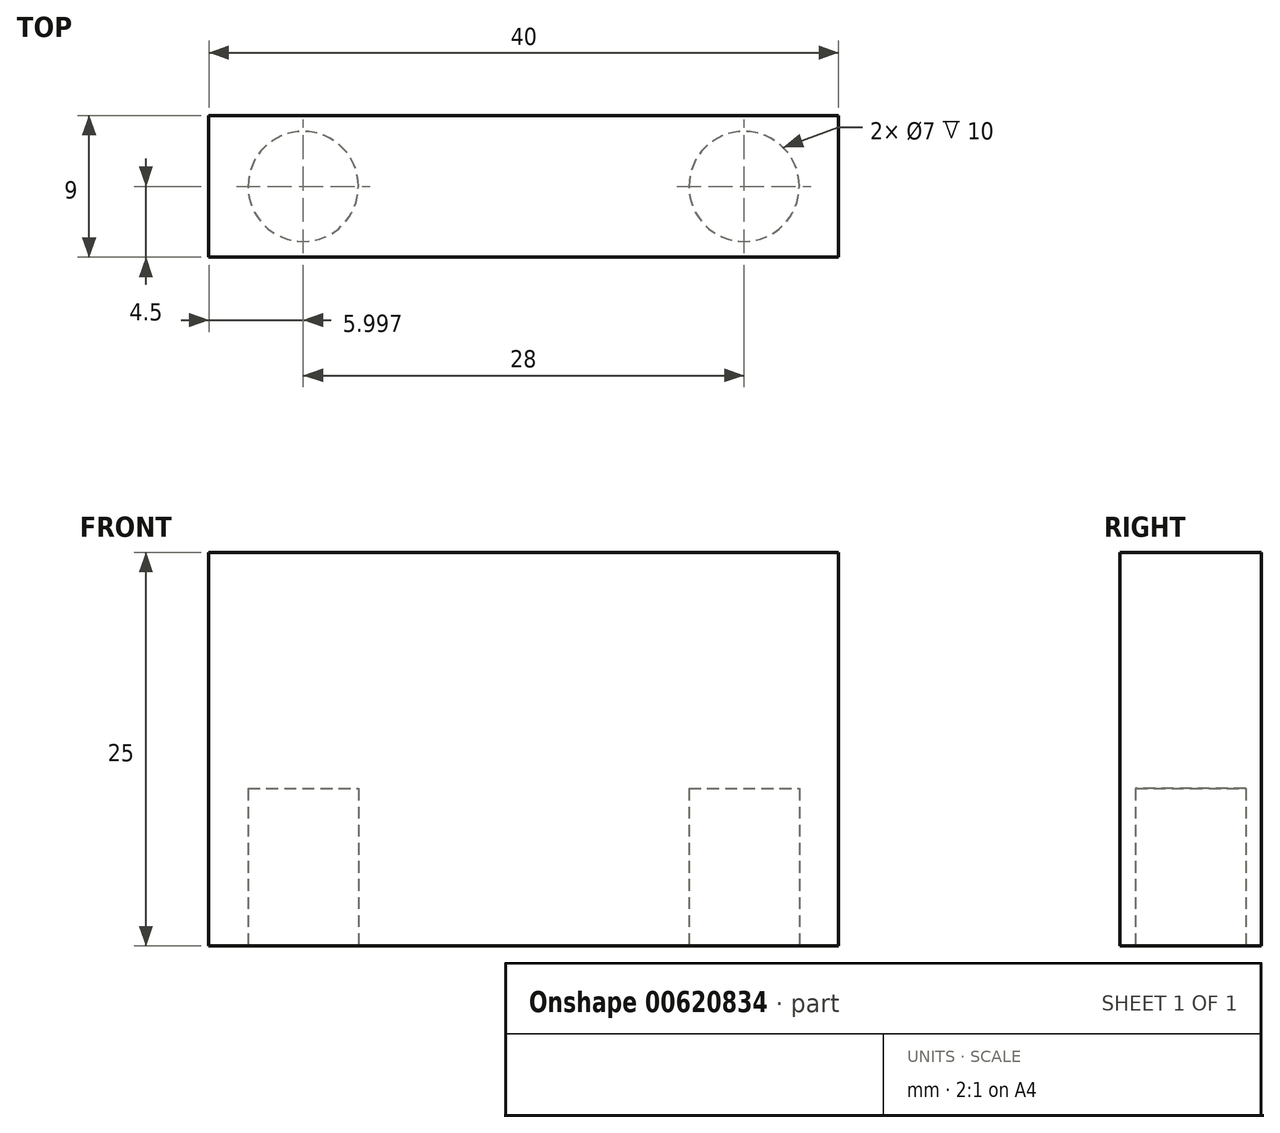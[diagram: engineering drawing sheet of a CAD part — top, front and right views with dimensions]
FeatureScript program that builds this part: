
annotation { "Feature Type Name" : "Feature", "Feature Type Description" : "" }
export const myFeature = defineFeature(function(context is Context, id is Id, definition is map)
    precondition{}
    {
        {
            var Q0;
            Q0=qCreatedBy(makeId("Front.planeOp"),FACE);
            cPlane(context, id + "F0", {"entities" : qUnion([Q0]), "cplaneType" : CPlaneType.OFFSET, "offset" : 25.4 * mm, "width" : 152.4 * mm, "height" : 152.4 * mm});
        }
        {
            var Q0;
            Q0=qCreatedBy(id+"F0.planeOp",FACE);
            var sketch = newSketch(context, id + "F1", { "sketchPlane" : qUnion([Q0])});
            skLineSegment(sketch, "E0.bottom", {"start": v(-14.75, 21.7) * mm, "end": v(25.25, 21.7) * mm});
            skLineSegment(sketch, "E0.top", {"start": v(-14.75, -3.3) * mm, "end": v(25.25, -3.3) * mm});
            skLineSegment(sketch, "E0.left", {"start": v(-14.75, 21.7) * mm, "end": v(-14.75, -3.3) * mm});
            skLineSegment(sketch, "E0.right", {"start": v(25.25, 21.7) * mm, "end": v(25.25, -3.3) * mm});
            skSolve(sketch);
        }
        {
            var Q0;
            Q0=makeQuery(id+"F1.imprint","IMPRINT",FACE,{"disambiguationData":[TD([[makeQuery(id+"F1.imprint","IMPRINT",EDGE,{"derivedFrom":sQuery(id+"F1.wireOp",EDGE,"E0.bottom")}),-1.0]])]});
            extrude(context, id + "F2", {"entities" : qUnion([Q0]), "depth" : 9 * mm, "offsetDistance" : 25.4 * mm});
        }
        {
            var Q0;
            Q0=makeQuery(id+"F2.opExtrude","SWEPT_FACE",FACE,{"disambiguationData":[OSD([sQuery(id+"F1.wireOp",EDGE,"E0.top")])]});
            var sketch = newSketch(context, id + "F3", { "sketchPlane" : qUnion([Q0])});
            skCircle(sketch, "E1", {"center": v(19.25, 29.9) * mm, "radius": 3.5 * mm});
            skCircle(sketch, "E2", {"center": v(-8.75, 29.9) * mm, "radius": 3.5 * mm});
            skSolve(sketch);
        }
        {
            var Q0;
            Q0=qSketchRegion(id+"F3",true);
            extrude(context, id + "F4", {"entities" : qUnion([Q0]), "operationType" : NewBodyOperationType.REMOVE, "oppositeDirection" : true, "depth" : 10 * mm, "offsetDistance" : 25.4 * mm});
        }
    });
